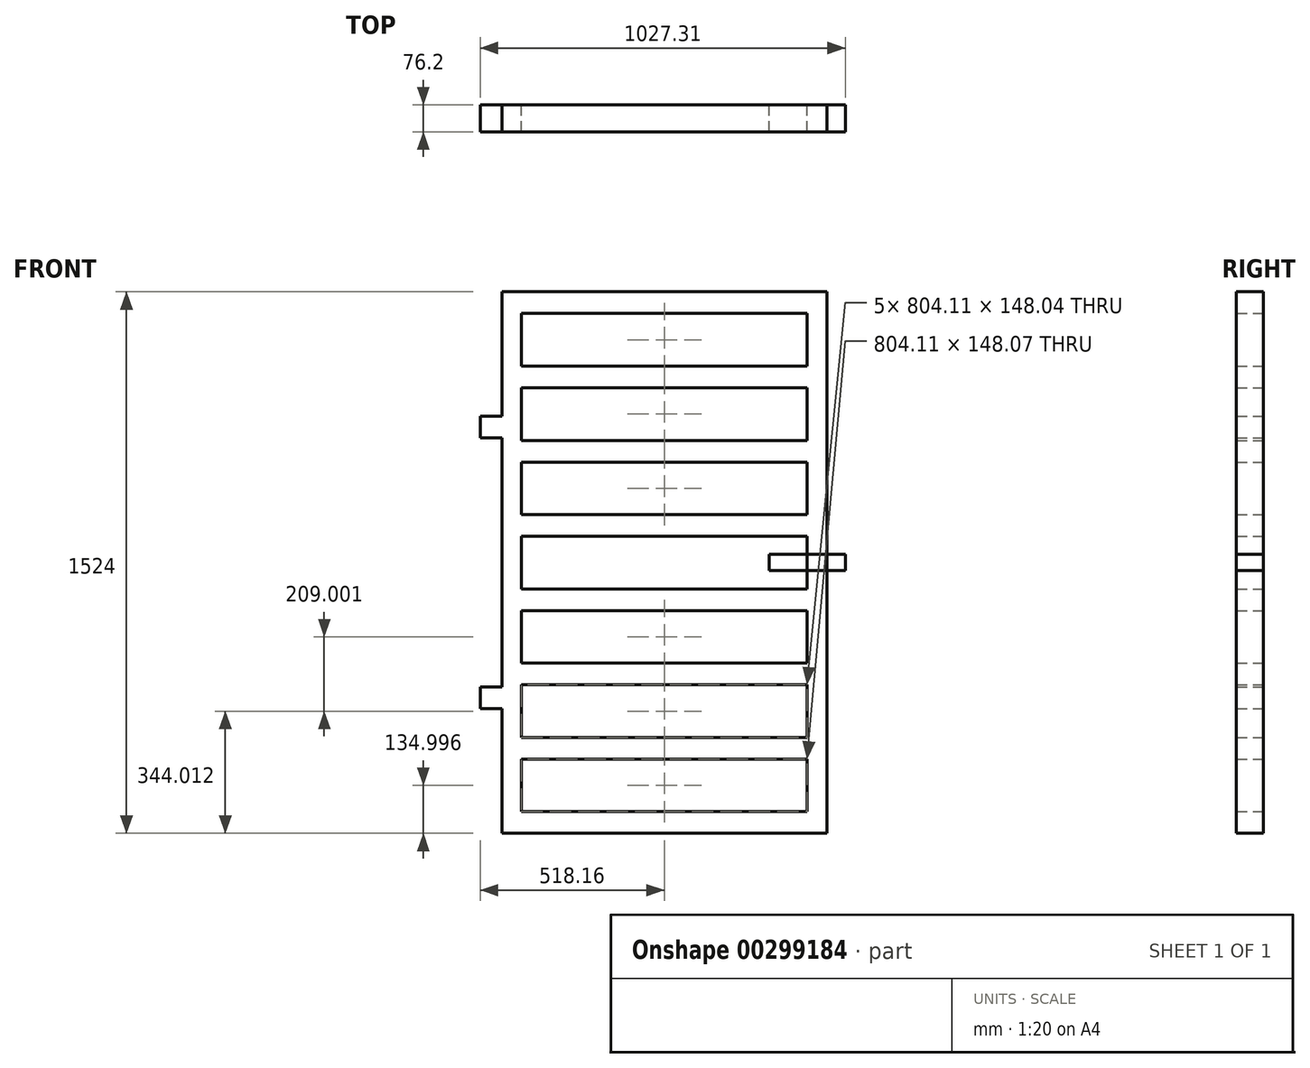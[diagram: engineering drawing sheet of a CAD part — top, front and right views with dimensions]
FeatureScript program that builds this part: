
annotation { "Feature Type Name" : "Feature", "Feature Type Description" : "" }
export const myFeature = defineFeature(function(context is Context, id is Id, definition is map)
    precondition{}
    {
        {
            var Q0;
            Q0=qCreatedBy(makeId("Front.planeOp"),FACE);
            var sketch = newSketch(context, id + "F0", { "sketchPlane" : qUnion([Q0])});
            skLineSegment(sketch, "E0.bottom", {"start": v(457.2, 762) * mm, "end": v(-457.2, 762) * mm});
            skLineSegment(sketch, "E0.top", {"start": v(457.2, -762) * mm, "end": v(-457.2, -762) * mm});
            skLineSegment(sketch, "E0.left", {"start": v(457.2, 762) * mm, "end": v(457.2, -762) * mm});
            skLineSegment(sketch, "E0.right", {"start": v(-457.2, 762) * mm, "end": v(-457.2, -762) * mm});
            skPoint(sketch, "E0.middle", {"position": v(0, 0) * mm});
            skLineSegment(sketch, "E1.bottom", {"start": v(402.06, 701.04) * mm, "end": v(-402.06, 701.04) * mm});
            skLineSegment(sketch, "E1.top", {"start": v(402.06, -701.04) * mm, "end": v(-402.06, -701.04) * mm});
            skLineSegment(sketch, "E1.left", {"start": v(402.06, 701.04) * mm, "end": v(402.06, -701.04) * mm});
            skLineSegment(sketch, "E1.right", {"start": v(-402.06, 701.04) * mm, "end": v(-402.06, -701.04) * mm});
            skLineSegment(sketch, "E2", {"start": v(-402.06, 553) * mm, "end": v(402.06, 553) * mm});
            skLineSegment(sketch, "E3", {"start": v(-402.06, 492.04) * mm, "end": v(402.06, 492.04) * mm});
            skLineSegment(sketch, "E4", {"start": v(-402.06, 553) * mm, "end": v(-402.06, 492.04) * mm});
            skLineSegment(sketch, "E5.bottom", {"start": v(-402.06, 344) * mm, "end": v(402.06, 344) * mm});
            skLineSegment(sketch, "E5.top", {"start": v(-402.06, 283.04) * mm, "end": v(402.06, 283.04) * mm});
            skLineSegment(sketch, "E5.left", {"start": v(-402.06, 344) * mm, "end": v(-402.06, 283.04) * mm});
            skLineSegment(sketch, "E5.right", {"start": v(402.06, 344) * mm, "end": v(402.06, 283.04) * mm});
            skLineSegment(sketch, "E6.bottom", {"start": v(-402.06, 135) * mm, "end": v(402.06, 135) * mm});
            skLineSegment(sketch, "E6.top", {"start": v(-402.06, 74.04) * mm, "end": v(402.06, 74.04) * mm});
            skLineSegment(sketch, "E6.left", {"start": v(-402.06, 135) * mm, "end": v(-402.06, 74.04) * mm});
            skLineSegment(sketch, "E6.right", {"start": v(402.06, 135) * mm, "end": v(402.06, 74.04) * mm});
            skLineSegment(sketch, "E7.bottom", {"start": v(-402.06, -74) * mm, "end": v(402.06, -74) * mm});
            skLineSegment(sketch, "E7.top", {"start": v(-402.06, -134.97) * mm, "end": v(402.06, -134.97) * mm});
            skLineSegment(sketch, "E7.left", {"start": v(-402.06, -74) * mm, "end": v(-402.06, -134.97) * mm});
            skLineSegment(sketch, "E7.right", {"start": v(402.06, -74) * mm, "end": v(402.06, -134.97) * mm});
            skLineSegment(sketch, "E8.bottom", {"start": v(-402.06, -283) * mm, "end": v(402.06, -283) * mm});
            skLineSegment(sketch, "E8.top", {"start": v(-402.06, -343.97) * mm, "end": v(402.06, -343.97) * mm});
            skLineSegment(sketch, "E8.left", {"start": v(-402.06, -283) * mm, "end": v(-402.06, -343.97) * mm});
            skLineSegment(sketch, "E8.right", {"start": v(402.06, -283) * mm, "end": v(402.06, -343.97) * mm});
            skLineSegment(sketch, "E9.bottom", {"start": v(-402.06, -492) * mm, "end": v(402.06, -492) * mm});
            skLineSegment(sketch, "E9.top", {"start": v(-402.06, -552.97) * mm, "end": v(402.06, -552.97) * mm});
            skLineSegment(sketch, "E9.left", {"start": v(-402.06, -492) * mm, "end": v(-402.06, -552.97) * mm});
            skLineSegment(sketch, "E9.right", {"start": v(402.06, -492) * mm, "end": v(402.06, -552.97) * mm});
            skLineSegment(sketch, "E10.bottom", {"start": v(-457.2, 411.48) * mm, "end": v(-518.16, 411.48) * mm});
            skLineSegment(sketch, "E10.top", {"start": v(-457.2, 350.52) * mm, "end": v(-518.16, 350.52) * mm});
            skLineSegment(sketch, "E10.left", {"start": v(-457.2, 411.48) * mm, "end": v(-457.2, 350.52) * mm});
            skLineSegment(sketch, "E10.right", {"start": v(-518.16, 411.48) * mm, "end": v(-518.16, 350.52) * mm});
            skLineSegment(sketch, "E11.bottom", {"start": v(-457.2, -350.52) * mm, "end": v(-518.16, -350.52) * mm});
            skLineSegment(sketch, "E11.top", {"start": v(-457.2, -411.48) * mm, "end": v(-518.16, -411.48) * mm});
            skLineSegment(sketch, "E11.left", {"start": v(-457.2, -350.52) * mm, "end": v(-457.2, -411.48) * mm});
            skLineSegment(sketch, "E11.right", {"start": v(-518.16, -350.52) * mm, "end": v(-518.16, -411.48) * mm});
            skLineSegment(sketch, "E12.bottom", {"start": v(509.15, -22.86) * mm, "end": v(294.96, -22.86) * mm});
            skLineSegment(sketch, "E12.top", {"start": v(509.15, 22.86) * mm, "end": v(294.96, 22.86) * mm});
            skLineSegment(sketch, "E12.left", {"start": v(509.15, -22.86) * mm, "end": v(509.15, 22.86) * mm});
            skLineSegment(sketch, "E12.right", {"start": v(294.96, -22.86) * mm, "end": v(294.96, 22.86) * mm});
            skPoint(sketch, "E12.middle", {"position": v(402.06, 0) * mm});
            skSolve(sketch);
        }
        {
            var Q0;
            {var subQ33=sQuery(id+"F0.wireOp",EDGE,"E0.bottom");Q0=makeQuery(id+"F0.imprint","IMPRINT",FACE,{"disambiguationData":[TD([[makeQuery(id+"F0.imprint","IMPRINT",EDGE,{"derivedFrom":subQ33}),1.0]])]});}
            var Q1;
            {var subQ0=sQuery(id+"F0.wireOp",EDGE,"E2");Q1=makeQuery(id+"F0.imprint","IMPRINT",FACE,{"disambiguationData":[TD([[makeQuery(id+"F0.imprint","IMPRINT",EDGE,{"derivedFrom":subQ0}),-1.0]])]});}
            var Q2;
            Q2=makeQuery(id+"F0.imprint","IMPRINT",FACE,{"disambiguationData":[TD([[makeQuery(id+"F0.imprint","IMPRINT",EDGE,{"derivedFrom":sQuery(id+"F0.wireOp",EDGE,"E5.bottom")}),-1.0]])]});
            var Q3;
            Q3=makeQuery(id+"F0.imprint","IMPRINT",FACE,{"disambiguationData":[TD([[makeQuery(id+"F0.imprint","IMPRINT",EDGE,{"derivedFrom":sQuery(id+"F0.wireOp",EDGE,"E6.bottom")}),-1.0]])]});
            var Q4;
            Q4=makeQuery(id+"F0.imprint","IMPRINT",FACE,{"disambiguationData":[TD([[makeQuery(id+"F0.imprint","IMPRINT",EDGE,{"derivedFrom":sQuery(id+"F0.wireOp",EDGE,"E7.bottom")}),-1.0]])]});
            var Q5;
            Q5=makeQuery(id+"F0.imprint","IMPRINT",FACE,{"disambiguationData":[TD([[makeQuery(id+"F0.imprint","IMPRINT",EDGE,{"derivedFrom":sQuery(id+"F0.wireOp",EDGE,"E8.bottom")}),-1.0]])]});
            var Q6;
            Q6=makeQuery(id+"F0.imprint","IMPRINT",FACE,{"disambiguationData":[TD([[makeQuery(id+"F0.imprint","IMPRINT",EDGE,{"derivedFrom":sQuery(id+"F0.wireOp",EDGE,"E9.bottom")}),-1.0]])]});
            var Q7;
            Q7=makeQuery(id+"F0.imprint","IMPRINT",FACE,{"disambiguationData":[TD([[makeQuery(id+"F0.imprint","IMPRINT",EDGE,{"derivedFrom":sQuery(id+"F0.wireOp",EDGE,"E11.bottom")}),1.0]])]});
            var Q8;
            Q8=makeQuery(id+"F0.imprint","IMPRINT",FACE,{"disambiguationData":[TD([[makeQuery(id+"F0.imprint","IMPRINT",EDGE,{"derivedFrom":sQuery(id+"F0.wireOp",EDGE,"E10.bottom")}),1.0]])]});
            var Q9;
            {var subQ5=sQuery(id+"F0.wireOp",EDGE,"E12.left");Q9=makeQuery(id+"F0.imprint","IMPRINT",FACE,{"disambiguationData":[TD([[makeQuery(id+"F0.imprint","IMPRINT",EDGE,{"derivedFrom":subQ5}),1.0]])]});}
            var Q10;
            {var subQ5=sQuery(id+"F0.wireOp",EDGE,"E12.right");Q10=makeQuery(id+"F0.imprint","IMPRINT",FACE,{"disambiguationData":[TD([[makeQuery(id+"F0.imprint","IMPRINT",EDGE,{"derivedFrom":subQ5}),-1.0]])]});}
            extrude(context, id + "F1", {"entities" : qUnion([Q0, Q1, Q2, Q3, Q4, Q5, Q6, Q7, Q8, Q9, Q10]), "depth" : 76.2 * mm});
        }
    });
